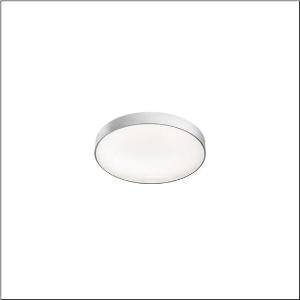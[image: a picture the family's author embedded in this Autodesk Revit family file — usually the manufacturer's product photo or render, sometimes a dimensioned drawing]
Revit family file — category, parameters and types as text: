
# Revit family: round_21_s_51mr34nd0321s
name_source: partatom
category: Lighting Fixtures
units: mm (PartAtom-declared; Revit-internal decimal feet)

## family parameters
Cut with Voids When Loaded = No
Host = Face
Light Source = No
Part Type = Normal
Room Calculation Point = No
Round Connector Dimension = Use Diameter
Shared = No

## types (1)
- Round 21 S (1 x LED, 3660 lm, 28.3 W, 3000K)
    Apparent Load = 28 VA
    CIE Flux Codes = 66 90 98 71 100
    Color Rendering = 80
    Color Temperature = 3000K
    Default Elevation = 1800 mm
    Description = Round 21 S, wall and ceiling luminaire, primary optical cover: micro prismatic cover, of PMMA, transparent, CAT 2 (L<= 3000cd/m²), light emission: direct/indirect distribution, primary light characteristic: symmetric, installation type: suspended mounting, surface-mounted, LED, rated luminous flux: 3.660lm, luminous efficacy: 129lm/W, light colour: 830, colour temperature: 3000K, control gear: DALI 2, with terminal, 5-pole, mains connection: 230V, AC, 50/60Hz, rated input power: 28.3W, housing, of aluminium, coated, silver, diameter: 400mm, height: 62mm, protection rating (complete): IP40, insulation class (complete): insulation class I (protective earthing), certification: CE, impact resistance: IK04, permissible operating ambient temperature: -10..+35°C, packaging unit: 1 piece
    Height = 87 mm
    Lamp = 1 x LED
    Lamp Light Flux = 3660 lm
    Lamp Power = 28.3 W
    Lamp count = 1
    Length = 400 mm
    Luminous efficacy = 129 lm/W
    Manufacturer = Siteco
    ModVariant = No
    Model = 51MR34ND0321S
    Mounting Place = Wall
    Mounting Type = Surface mounted
    Number of Poles = 1
    OnlyDefault = Yes
    Power Factor = 1
    Product Name = Round 21 S
    Product group = wall and ceiling luminaire
    ProductGroupID = 2001
    Protection Class = Protection class I
    Protection Degree = IP 40
    RLX_Detail_Level = 1
    RLX_Emergency_Light_Flux = 0 lm
    RLX_Emergency_Type = 0
    RLX_Emergency_Type_DB = No
    RlxData = <blob elided: 15129 chars, md5=5a7e293a>
    Socket = socket
    Standby Power = 0 W
    System Light Flux = 3660 lm
    System Power = 28 W
    Type Comments = Product without accessories
    Type Image = l_1258336.jpg
    URL = http://relux.com
    VarID = ---
    Voltage = 0 V
    Weight = 0.00 kg
    Width = 0 mm  [stored 0 ft]

note: [stored X ft] marks values corroborated as IEEE doubles in the binary element streams (Revit-internal decimal feet)

## geometry (parser evidence)
native form markers: Blend x4, Sweep x13
no freeform markers — native parametric forms only
